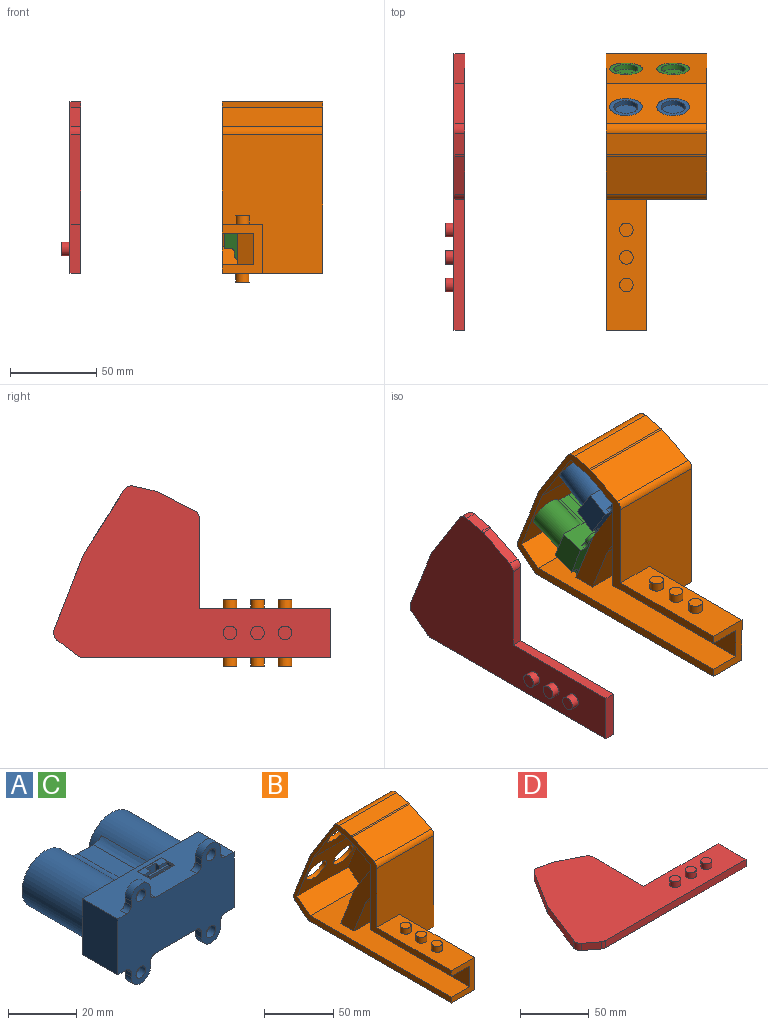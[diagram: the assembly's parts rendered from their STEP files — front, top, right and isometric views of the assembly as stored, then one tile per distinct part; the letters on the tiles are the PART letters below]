
ASSEMBLY  parts=4 mates=8
PART A: 74 faces, bbox 48x40x35.5 mm
  f0: plane 48x14.5mm, normal (0,0,1), area 581mm2, adj f10,f11,f12,f17,f22,f37,f38,f39
  f1: extruded ~22.5x3.45mm, area 88mm2, adj f2,f42,f43,f44
  f2: plane 22.5x6.46mm, normal (0,0,1), area 145.3mm2, adj f1,f3,f43,f44
  f3: extruded ~22.5x3.45mm, area 88mm2, adj f2,f41,f43,f44
  f4: extruded ~22.5x3.45mm, area 88mm2, adj f5,f41,f43,f44
  f5: plane 22.5x6.46mm, normal (0,0,-1), area 145.3mm2, adj f4,f6,f43,f44
  f6: extruded ~22.5x3.45mm, area 88mm2, adj f5,f42,f43,f44
  f7: plane 19x19mm, normal (0,1,0), area 129.6mm2, adj f42,f45
  f8: plane 19x19mm, normal (0,1,0), area 129.6mm2, adj f41,f46
  f9: plane 48x14.5mm, normal (0,0,-1), area 636mm2, adj f10,f11,f12,f27,f32,f33,f34,f35
  f10: plane 20x14.5mm, normal (-1,0,0), area 290mm2, adj f0,f9,f12,f43
  f11: plane 20x14.5mm, normal (1,0,0), area 290mm2, adj f0,f9,f12,f43
  f12: plane 48x35.52mm, normal (0,-1,0), area 1137.5mm2, adj f0,f9,f10,f11,f13,f14,f15,f16
  f13: plane 2.5x1.5mm, normal (-1,0,0), area 3.8mm2, adj f12,f14,f17,f40
  f14: cylinder r=4.01mm len=8.01mm, axis (0,-1,0), area 31.5mm2, adj f12,f13,f15,f17
  f15: plane 2.5x2mm, normal (1,0,0), area 5mm2, adj f12,f14,f17,f39
  f16: cylinder r=2mm len=4mm, axis (0,-1,0), area 31.4mm2, adj f12,f17
  f17: plane 12x7.76mm, normal (0,1,0), area 44.4mm2, adj f0,f13,f14,f15,f16,f39,f40
  f18: cylinder r=4.01mm len=8.01mm, axis (0,-1,0), area 31.5mm2, adj f12,f19,f20,f22
  f19: plane 2.5x1.5mm, normal (1,0,0), area 3.8mm2, adj f12,f18,f22,f38
  f20: plane 2.5x2mm, normal (-1,0,0), area 5mm2, adj f12,f18,f22,f37
  f21: cylinder r=2mm len=4mm, axis (0,-1,0), area 31.4mm2, adj f12,f22
  f22: plane 12x7.76mm, normal (0,1,0), area 44.4mm2, adj f0,f18,f19,f20,f21,f37,f38
  f23: cylinder r=4.01mm len=8.01mm, axis (0,-1,0), area 31.5mm2, adj f12,f24,f25,f27
  f24: plane 2.5x1.5mm, normal (-1,0,0), area 3.8mm2, adj f12,f23,f27,f36
  f25: plane 2.5x2mm, normal (1,0,0), area 5mm2, adj f12,f23,f27,f35
  f26: cylinder r=2mm len=4mm, axis (0,-1,0), area 31.4mm2, adj f12,f27
  f27: plane 12x7.76mm, normal (0,1,0), area 44.4mm2, adj f9,f23,f24,f25,f26,f35,f36
  f28: plane 2.5x1.5mm, normal (1,0,0), area 3.8mm2, adj f12,f29,f32,f33
  f29: cylinder r=4.01mm len=8.01mm, axis (0,-1,0), area 31.5mm2, adj f12,f28,f30,f32
  f30: plane 2.5x2mm, normal (-1,0,0), area 5mm2, adj f12,f29,f32,f34
  f31: cylinder r=2mm len=4mm, axis (0,-1,0), area 31.4mm2, adj f12,f32
  f32: plane 12x7.76mm, normal (0,1,0), area 44.4mm2, adj f9,f28,f29,f30,f31,f33,f34
  f33: cylinder r=2mm len=2.5mm, axis (0,-1,0), area 7.9mm2, adj f9,f12,f28,f32
  f34: cylinder r=2mm len=2.5mm, axis (0,1,0), area 7.9mm2, adj f9,f12,f30,f32
  f35: cylinder r=2mm len=2.5mm, axis (0,-1,0), area 7.9mm2, adj f9,f12,f25,f27
  f36: cylinder r=2mm len=2.5mm, axis (0,1,0), area 7.9mm2, adj f9,f12,f24,f27
  f37: cylinder r=2mm len=2.5mm, axis (0,1,0), area 7.9mm2, adj f0,f12,f20,f22
  f38: cylinder r=2mm len=2.5mm, axis (0,-1,0), area 7.9mm2, adj f0,f12,f19,f22
  f39: cylinder r=2mm len=2.5mm, axis (0,-1,0), area 7.9mm2, adj f0,f12,f15,f17
  f40: cylinder r=2mm len=2.5mm, axis (0,1,0), area 7.9mm2, adj f0,f12,f13,f17
  f41: cylinder r=9.5mm len=25.5mm, axis (0,1,0), area 1209.4mm2, adj f3,f4,f8,f43,f44
  f42: cylinder r=9.5mm len=25.5mm, axis (0,1,0), area 1209.4mm2, adj f1,f6,f7,f43,f44
  f43: plane 48x20mm, normal (0,1,0), area 301.3mm2, adj f0,f1,f2,f3,f4,f5,f6,f9
  f44: plane 13.36x12.69mm, normal (0,1,0), area 91.6mm2, adj f1,f2,f3,f4,f5,f6,f41,f42
  f45: cylinder r=7mm len=14mm, axis (0,1,0), area 131.9mm2, adj f7,f47
  f46: cylinder r=7mm len=14mm, axis (0,1,0), area 131.9mm2, adj f8,f48
  f47: plane 14x14mm, normal (0,1,0), area 153.9mm2, adj f45
  f48: plane 14x14mm, normal (0,1,0), area 153.9mm2, adj f46
  f49: plane 5.5x0.1mm, normal (1,0,0), area 0.5mm2, adj f0,f50,f52,f53
  f50: plane 10x0.1mm, normal (0,-1,0), area 1mm2, adj f0,f49,f51,f53
  f51: plane 5.5x0.1mm, normal (-1,0,0), area 0.5mm2, adj f0,f50,f52,f53
  f52: plane 10x0.1mm, normal (0,1,0), area 1mm2, adj f0,f49,f51,f53
  f53: plane 10x5.5mm, normal (0,0,1), area 24.8mm2, adj f49,f50,f51,f52,f54,f55,f56,f57
  f54: plane 3.9x2.62mm, normal (0,-1,0), area 10.2mm2, adj f53,f55,f61,f62
  f55: plane 3.9x2.55mm, normal (1,0,0), area 9.9mm2, adj f53,f54,f56,f62
  f56: plane 9.25x3.9mm, normal (0,1,0), area 36.1mm2, adj f53,f55,f57,f62
  f57: plane 3.9x2.55mm, normal (-1,0,0), area 9.9mm2, adj f53,f56,f58,f62
  f58: plane 3.9x2.82mm, normal (0,-1,0), area 11mm2, adj f53,f57,f59,f62
  f59: plane 3.9x1.75mm, normal (-1,0,0), area 6.8mm2, adj f53,f58,f60,f62
  f60: plane 3.9x3.81mm, normal (0,-1,0), area 14.8mm2, adj f53,f59,f61,f62
  f61: plane 3.9x1.75mm, normal (1,0,0), area 6.8mm2, adj f53,f54,f60,f62
  f62: plane 9.25x4.3mm, normal (0,0,1), area 24.3mm2, adj f54,f55,f56,f57,f58,f59,f60,f61
  f63: plane 3.9x0.71mm, normal (1,0,0), area 2.8mm2, adj f62,f64,f66,f67
  f64: plane 8.36x3.9mm, normal (0,-1,0), area 32.6mm2, adj f62,f63,f65,f67
  f65: plane 3.9x0.71mm, normal (-1,0,0), area 2.8mm2, adj f62,f64,f66,f67
  f66: plane 8.36x3.9mm, normal (0,1,0), area 32.6mm2, adj f62,f63,f65,f67
  f67: plane 8.36x0.71mm, normal (0,0,1), area 5.9mm2, adj f63,f64,f65,f66
  f68: plane 14x14mm, normal (0,-1,0), area 153.9mm2, adj f70
  f69: plane 14x14mm, normal (0,1,0), area 153.9mm2, adj f70
  f70: cylinder r=7mm len=20.5mm, axis (0,1,0), area 901.6mm2, adj f68,f69
  f71: plane 14x14mm, normal (0,-1,0), area 153.9mm2, adj f73
  f72: plane 14x14mm, normal (0,1,0), area 153.9mm2, adj f73
  f73: cylinder r=7mm len=20.5mm, axis (0,1,0), area 901.6mm2, adj f71,f72
PART B: 49 faces, bbox 58.5x160.9x104.8 mm
  f0: plane 52.14x21.04mm, normal (0,0.45,-0.89), area 1222.8mm2, adj f1,f2,f8,f22,f29,f30
  f1: plane 90.19x74.88mm, normal (-1,0,0), area 3409mm2, adj f0,f3,f19,f20,f21,f22,f27,f30
  f2: plane 76.26x52.14mm, normal (0,1,0), area 2619.3mm2, adj f0,f3,f4,f8,f9,f10,f26,f29
  f3: plane 144.07x52.14mm, normal (0,0,1), area 4139.2mm2, adj f1,f2,f4,f8,f10,f11,f19,f27
  f4: plane 52.69x25.72mm, normal (-1,0,0), area 757.8mm2, adj f2,f3,f26,f28
  f5: plane 76.2x28.58mm, normal (1,0,0), area 2177.4mm2, adj f6,f7,f11,f13
  f6: plane 76.2x23.5mm, normal (0,0,1), area 1641.9mm2, adj f5,f8,f11,f13,f35,f37,f39
  f7: plane 144.07x58.49mm, normal (0,0,-1), area 5611.5mm2, adj f5,f8,f11,f12,f13,f41,f43,f45
  f8: plane 160.93x99.73mm, normal (-1,0,0), area 2078.4mm2, adj f0,f2,f3,f6,f7,f9,f11,f13
  f9: plane 82.55x18.42mm, normal (0,0,-1), area 1520.2mm2, adj f2,f8,f10,f11
  f10: plane 82.55x18.42mm, normal (-1,0,0), area 1520.2mm2, adj f2,f3,f9,f11
  f11: plane 28.58x23.5mm, normal (0,-1,0), area 332.3mm2, adj f3,f5,f6,f7,f8,f9,f10
  f12: plane 99.73x84.73mm, normal (1,0,0), area 6510.9mm2, adj f7,f13,f14,f15,f16,f17,f18,f23
  f13: plane 80.7x58.49mm, normal (0,-1,0), area 4048.9mm2, adj f5,f6,f7,f8,f12,f24
  f14: plane 58.49x12.56mm, normal (0,-0.23,0.97), area 753.7mm2, adj f8,f12,f23,f25
  f15: plane 58.49x21.79mm, normal (0,-0.45,0.89), area 1429mm2, adj f8,f12,f23,f24
  f16: plane 58.49x11.79mm, normal (0,0.61,-0.79), area 869.7mm2, adj f8,f12,f47,f48
  f17: plane 58.49x43.78mm, normal (0,0.93,0.36), area 2181.5mm2, adj f8,f12,f18,f33,f34,f47
  f18: plane 58.49x37.57mm, normal (0,0.85,0.53), area 2028.2mm2, adj f8,f12,f17,f25,f31,f32
  f19: plane 52.14x13.51mm, normal (0,-0.61,0.79), area 888.4mm2, adj f1,f3,f8,f20
  f20: plane 52.14x42.95mm, normal (0,-0.93,-0.36), area 1836.6mm2, adj f1,f8,f19,f21,f33,f34
  f21: plane 52.14x36.85mm, normal (0,-0.85,-0.53), area 1701.6mm2, adj f1,f8,f20,f22,f31,f32
  f22: plane 52.14x14.11mm, normal (0,0.23,-0.97), area 755mm2, adj f0,f1,f8,f21
  f23: cylinder r=5.08mm len=58.49mm, axis (-1,0,0), area 72mm2, adj f8,f12,f14,f15
  f24: cylinder r=5.08mm len=58.49mm, axis (-1,0,0), area 327.3mm2, adj f8,f12,f13,f15
  f25: cylinder r=5.08mm len=58.49mm, axis (1,0,0), area 367.6mm2, adj f8,f12,f14,f18
  f26: plane 43.18x21.79mm, normal (0,-0.85,-0.53), area 1110.9mm2, adj f2,f4,f28,f29
  f27: plane 43.18x36.63mm, normal (0,0.93,0.36), area 1697.7mm2, adj f1,f3,f29,f30
  f28: plane 43.18x30.9mm, normal (0,-0.93,-0.36), area 1431.9mm2, adj f3,f4,f26,f29
  f29: plane 76.34x39.35mm, normal (-1,0,0), area 923mm2, adj f0,f2,f3,f26,f27,f28,f30
  f30: plane 43.18x39.7mm, normal (0,0.85,0.53), area 2024.5mm2, adj f0,f1,f27,f29
  f31: cylinder r=9.5mm len=19mm, axis (0,0.85,0.53), area 178.9mm2, adj f18,f21
  f32: cylinder r=9.5mm len=19mm, axis (0,0.85,0.53), area 178.9mm2, adj f18,f21
  f33: cylinder r=9.5mm len=19mm, axis (0,0.93,0.36), area 178.9mm2, adj f17,f20
  f34: cylinder r=9.5mm len=19mm, axis (0,0.93,0.36), area 178.9mm2, adj f17,f20
  f35: cylinder r=3.97mm len=7.94mm, axis (0,0,-1), area 126.7mm2, adj f6,f36
  f36: plane 7.94x7.94mm, normal (0,0,1), area 49.5mm2, adj f35
  f37: cylinder r=3.97mm len=7.94mm, axis (0,0,-1), area 126.7mm2, adj f6,f38
  f38: plane 7.94x7.94mm, normal (0,0,1), area 49.5mm2, adj f37
  f39: cylinder r=3.97mm len=7.94mm, axis (0,0,-1), area 126.7mm2, adj f6,f40
  f40: plane 7.94x7.94mm, normal (0,0,1), area 49.5mm2, adj f39
  f41: cylinder r=3.97mm len=7.94mm, axis (0,0,1), area 126.7mm2, adj f7,f42
  f42: plane 7.94x7.94mm, normal (0,0,-1), area 49.5mm2, adj f41
  f43: cylinder r=3.97mm len=7.94mm, axis (0,0,1), area 126.7mm2, adj f7,f44
  f44: plane 7.94x7.94mm, normal (0,0,-1), area 49.5mm2, adj f43
  f45: cylinder r=3.97mm len=7.94mm, axis (0,0,1), area 126.7mm2, adj f7,f46
  f46: plane 7.94x7.94mm, normal (0,0,-1), area 49.5mm2, adj f45
  f47: cylinder r=5.08mm len=58.49mm, axis (-1,0,0), area 382.3mm2, adj f8,f12,f16,f17
  f48: cylinder r=5.08mm len=58.49mm, axis (-1,0,0), area 194.8mm2, adj f7,f8,f12,f16
PART C: same geometry as A
PART D: 22 faces, bbox 160.9x99.7x11.4 mm
  f0: plane 144.07x6.35mm, normal (0,-1,0), area 914.8mm2, adj f1,f13,f14,f15
  f1: plane 28.58x6.35mm, normal (1,0,0), area 181.5mm2, adj f0,f2,f14,f15
  f2: plane 76.2x6.35mm, normal (0,1,0), area 483.9mm2, adj f1,f3,f14,f15
  f3: plane 52.13x6.35mm, normal (1,0,0), area 331mm2, adj f2,f4,f14,f15
  f4: cylinder r=5.08mm len=6.35mm, axis (0,0,-1), area 35.5mm2, adj f3,f5,f14,f15
  f5: plane 21.79x11.05mm, normal (0.45,0.89,0), area 155.1mm2, adj f4,f6,f14,f15
  f6: cylinder r=5.08mm len=6.35mm, axis (0,0,-1), area 7.8mm2, adj f5,f7,f14,f15
  f7: plane 12.56x6.35mm, normal (0.23,0.97,0), area 81.8mm2, adj f6,f8,f14,f15
  f8: cylinder r=5.08mm len=6.35mm, axis (0,0,-1), area 39.9mm2, adj f7,f9,f14,f15
  f9: plane 37.57x23.6mm, normal (-0.85,0.53,0), area 281.8mm2, adj f8,f10,f14,f15
  f10: plane 43.78x17.06mm, normal (-0.93,0.36,0), area 298.4mm2, adj f9,f11,f14,f15
  f11: cylinder r=5.08mm len=6.35mm, axis (0,0,-1), area 41.5mm2, adj f10,f12,f14,f15
  f12: plane 11.79x9.07mm, normal (-0.61,-0.79,0), area 94.4mm2, adj f11,f13,f14,f15
  f13: cylinder r=5.08mm len=6.35mm, axis (0,0,-1), area 21.2mm2, adj f0,f12,f14,f15
  f14: plane 160.93x99.73mm, normal (0,0,1), area 8539.9mm2, adj f0,f1,f2,f3,f4,f5,f6,f7
  f15: plane 160.93x99.73mm, normal (0,0,-1), area 8688.4mm2, adj f0,f1,f2,f3,f4,f5,f6,f7
  f16: cylinder r=3.97mm len=7.94mm, axis (0,0,-1), area 126.7mm2, adj f14,f17
  f17: plane 7.94x7.94mm, normal (0,0,1), area 49.5mm2, adj f16
  f18: cylinder r=3.97mm len=7.94mm, axis (0,0,-1), area 126.7mm2, adj f14,f19
  f19: plane 7.94x7.94mm, normal (0,0,1), area 49.5mm2, adj f18
  f20: cylinder r=3.97mm len=7.94mm, axis (0,0,-1), area 126.7mm2, adj f14,f21
  f21: plane 7.94x7.94mm, normal (0,0,1), area 49.5mm2, adj f20
PLACE A rot(axis=(1,0,0),32.1deg) t=(-41.48,184.45,-93.69)mm
PLACE B t=(-48.16,83.32,-145.76)mm
PLACE C rot(axis=(1,0,0),21.3deg) t=(-41.48,201.57,-131.29)mm
PLACE D rot(axis=(0.58,-0.58,-0.58),120deg) t=(-125.18,82.42,146.5)mm
MATE cylindrical A.f42 <-> B.f32  axis (0,0.85,0.53) through (-31.58,202.27,-70.82)mm
MATE planar D.f0 <-> B.f7  axis (0,0,-1) through (-128.35,155.36,-145.76)mm
MATE planar A.f44 <-> B.f21  axis (0,0.85,0.53) through (-17.83,210.52,-65.63)mm
MATE cylindrical C.f41 <-> B.f34  axis (0,0.93,0.36) through (-4.08,211.49,-116.81)mm
MATE planar C.f44 <-> B.f20  axis (0,0.93,0.36) through (-17.83,230.73,-104.21)mm
MATE planar D.f10 <-> B.f17  axis (0,0.93,0.36) through (-128.35,235.38,-107.88)mm
MATE cylindrical C.f42 <-> B.f33  axis (0,0.93,0.36) through (-31.58,223.37,-112.18)mm
MATE cylindrical A.f41 <-> B.f31  axis (0,0.85,0.53) through (-4.08,202.27,-70.82)mm
